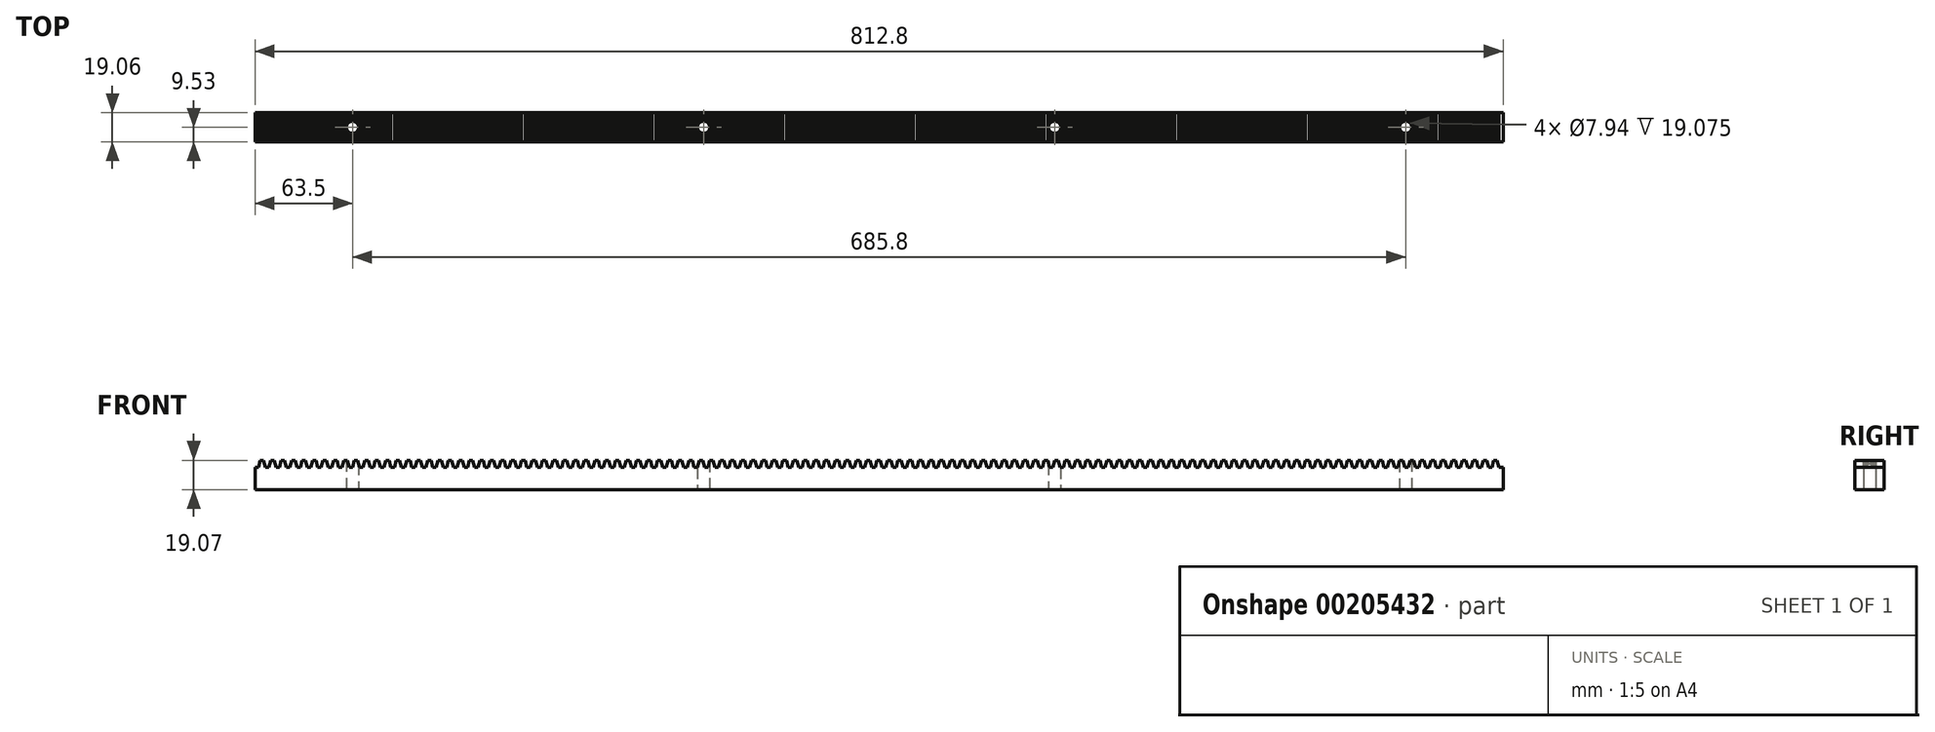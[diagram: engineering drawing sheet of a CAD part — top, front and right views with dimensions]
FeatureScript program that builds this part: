
annotation { "Feature Type Name" : "Feature", "Feature Type Description" : "" }
export const myFeature = defineFeature(function(context is Context, id is Id, definition is map)
    precondition{}
    {
        {
            var Q0;
            Q0=qCreatedBy(makeId("Right.planeOp"),FACE);
            var sketch = newSketch(context, id + "F0", { "sketchPlane" : qUnion([Q0])});
            skLineSegment(sketch, "E0.bottom", {"start": v(-9.52, 7.25) * mm, "end": v(9.53, 7.25) * mm});
            skLineSegment(sketch, "E0.top", {"start": v(-9.53, -7.25) * mm, "end": v(9.52, -7.25) * mm});
            skLineSegment(sketch, "E0.left", {"start": v(-9.52, 7.25) * mm, "end": v(-9.53, -7.25) * mm});
            skLineSegment(sketch, "E0.right", {"start": v(9.53, 7.25) * mm, "end": v(9.52, -7.25) * mm});
            skPoint(sketch, "E0.middle", {"position": v(0, 0) * mm});
            skSolve(sketch);
        }
        {
            var Q0;
            Q0 = qSketchRegion(id + "F0", true);
            extrude(context, id + "F1", {"entities" : qUnion([Q0]), "endBound" : BoundingType.SYMMETRIC, "depth" : 812.8 * mm});
        }
        {
            var Q0;
            Q0=makeQuery(id+"F1.opExtrude","SWEPT_FACE",FACE,{"disambiguationData":[OSD([sQuery(id+"F0.wireOp",EDGE,"E0.left")])]});
            var sketch = newSketch(context, id + "F2", { "sketchPlane" : qUnion([Q0])});
            skLineSegment(sketch, "E1.0", {"start": v(406.4, 7.25) * mm, "end": v(-406.4, 7.25) * mm});
            skLineSegment(sketch, "E2.0", {"start": v(406.4, 11.82) * mm, "end": v(-406.4, 11.82) * mm, "construction": true});
            skLineSegment(sketch, "E3", {"start": v(-406.4, 7.25) * mm, "end": v(-406.4, 19.13) * mm, "construction": true});
            skLineSegment(sketch, "E4.0", {"start": v(-404.16, 7.25) * mm, "end": v(-404.16, 19.13) * mm, "construction": true});
            skLineSegment(sketch, "E5.0", {"start": v(-403, 7.25) * mm, "end": v(-403, 19.13) * mm, "construction": true});
            skLineSegment(sketch, "E6.0", {"start": v(-400.76, 7.25) * mm, "end": v(-400.76, 19.13) * mm, "construction": true});
            skLineSegment(sketch, "E7.0", {"start": v(-399.6, 7.25) * mm, "end": v(-399.6, 19.13) * mm, "construction": true});
            skLineSegment(sketch, "E8", {"start": v(-406.4, 7.25) * mm, "end": v(-404.16, 7.25) * mm});
            skLineSegment(sketch, "E9", {"start": v(-403, 11.82) * mm, "end": v(-404.16, 7.25) * mm});
            skLineSegment(sketch, "E10", {"start": v(-403, 11.82) * mm, "end": v(-400.76, 11.82) * mm});
            skLineSegment(sketch, "E11", {"start": v(-400.76, 11.82) * mm, "end": v(-399.6, 7.25) * mm});
            skLineSegment(sketch, "E12.1.0.0", {"start": v(-399.6, 7.25) * mm, "end": v(-397.36, 7.25) * mm});
            skLineSegment(sketch, "E12.1.0.1", {"start": v(-393.95, 11.82) * mm, "end": v(-392.79, 7.25) * mm});
            skLineSegment(sketch, "E12.1.0.2", {"start": v(-396.19, 11.82) * mm, "end": v(-393.95, 11.82) * mm});
            skLineSegment(sketch, "E12.1.0.3", {"start": v(-396.19, 11.82) * mm, "end": v(-397.36, 7.25) * mm});
            skLineSegment(sketch, "E12.2.0.0", {"start": v(-392.79, 7.25) * mm, "end": v(-390.55, 7.25) * mm});
            skLineSegment(sketch, "E12.2.0.1", {"start": v(-387.15, 11.82) * mm, "end": v(-385.98, 7.25) * mm});
            skLineSegment(sketch, "E12.2.0.2", {"start": v(-389.38, 11.82) * mm, "end": v(-387.15, 11.82) * mm});
            skLineSegment(sketch, "E12.2.0.3", {"start": v(-389.38, 11.82) * mm, "end": v(-390.55, 7.25) * mm});
            skLineSegment(sketch, "E12.3.0.0", {"start": v(-385.98, 7.25) * mm, "end": v(-383.74, 7.25) * mm});
            skLineSegment(sketch, "E12.3.0.1", {"start": v(-380.34, 11.82) * mm, "end": v(-379.17, 7.25) * mm});
            skLineSegment(sketch, "E12.3.0.2", {"start": v(-382.57, 11.82) * mm, "end": v(-380.34, 11.82) * mm});
            skLineSegment(sketch, "E12.3.0.3", {"start": v(-382.57, 11.82) * mm, "end": v(-383.74, 7.25) * mm});
            skLineSegment(sketch, "E12.4.0.0", {"start": v(-379.17, 7.25) * mm, "end": v(-376.94, 7.25) * mm});
            skLineSegment(sketch, "E12.4.0.1", {"start": v(-373.53, 11.82) * mm, "end": v(-372.36, 7.25) * mm});
            skLineSegment(sketch, "E12.4.0.2", {"start": v(-375.77, 11.82) * mm, "end": v(-373.53, 11.82) * mm});
            skLineSegment(sketch, "E12.4.0.3", {"start": v(-375.77, 11.82) * mm, "end": v(-376.94, 7.25) * mm});
            skLineSegment(sketch, "E12.5.0.0", {"start": v(-372.36, 7.25) * mm, "end": v(-370.13, 7.25) * mm});
            skLineSegment(sketch, "E12.5.0.1", {"start": v(-366.73, 11.82) * mm, "end": v(-365.56, 7.25) * mm});
            skLineSegment(sketch, "E12.5.0.2", {"start": v(-368.96, 11.82) * mm, "end": v(-366.73, 11.82) * mm});
            skLineSegment(sketch, "E12.5.0.3", {"start": v(-368.96, 11.82) * mm, "end": v(-370.13, 7.25) * mm});
            skLineSegment(sketch, "E12.6.0.0", {"start": v(-365.56, 7.25) * mm, "end": v(-363.32, 7.25) * mm});
            skLineSegment(sketch, "E12.6.0.1", {"start": v(-359.92, 11.82) * mm, "end": v(-358.75, 7.25) * mm});
            skLineSegment(sketch, "E12.6.0.2", {"start": v(-362.15, 11.82) * mm, "end": v(-359.92, 11.82) * mm});
            skLineSegment(sketch, "E12.6.0.3", {"start": v(-362.15, 11.82) * mm, "end": v(-363.32, 7.25) * mm});
            skLineSegment(sketch, "E12.7.0.0", {"start": v(-358.75, 7.25) * mm, "end": v(-356.51, 7.25) * mm});
            skLineSegment(sketch, "E12.7.0.1", {"start": v(-353.11, 11.82) * mm, "end": v(-351.94, 7.25) * mm});
            skLineSegment(sketch, "E12.7.0.2", {"start": v(-355.35, 11.82) * mm, "end": v(-353.11, 11.82) * mm});
            skLineSegment(sketch, "E12.7.0.3", {"start": v(-355.35, 11.82) * mm, "end": v(-356.51, 7.25) * mm});
            skLineSegment(sketch, "E12.8.0.0", {"start": v(-351.94, 7.25) * mm, "end": v(-349.7, 7.25) * mm});
            skLineSegment(sketch, "E12.8.0.1", {"start": v(-346.3, 11.82) * mm, "end": v(-345.14, 7.25) * mm});
            skLineSegment(sketch, "E12.8.0.2", {"start": v(-348.54, 11.82) * mm, "end": v(-346.3, 11.82) * mm});
            skLineSegment(sketch, "E12.8.0.3", {"start": v(-348.54, 11.82) * mm, "end": v(-349.7, 7.25) * mm});
            skLineSegment(sketch, "E12.9.0.0", {"start": v(-345.14, 7.25) * mm, "end": v(-342.9, 7.25) * mm});
            skLineSegment(sketch, "E12.9.0.1", {"start": v(-339.5, 11.82) * mm, "end": v(-338.33, 7.25) * mm});
            skLineSegment(sketch, "E12.9.0.2", {"start": v(-341.73, 11.82) * mm, "end": v(-339.5, 11.82) * mm});
            skLineSegment(sketch, "E12.9.0.3", {"start": v(-341.73, 11.82) * mm, "end": v(-342.9, 7.25) * mm});
            skLineSegment(sketch, "E12.10.0.0", {"start": v(-338.33, 7.25) * mm, "end": v(-336.1, 7.25) * mm});
            skLineSegment(sketch, "E12.10.0.1", {"start": v(-332.69, 11.82) * mm, "end": v(-331.52, 7.25) * mm});
            skLineSegment(sketch, "E12.10.0.2", {"start": v(-334.92, 11.82) * mm, "end": v(-332.69, 11.82) * mm});
            skLineSegment(sketch, "E12.10.0.3", {"start": v(-334.92, 11.82) * mm, "end": v(-336.1, 7.25) * mm});
            skLineSegment(sketch, "E12.11.0.0", {"start": v(-331.52, 7.25) * mm, "end": v(-329.29, 7.25) * mm});
            skLineSegment(sketch, "E12.11.0.1", {"start": v(-325.88, 11.82) * mm, "end": v(-324.71, 7.25) * mm});
            skLineSegment(sketch, "E12.11.0.2", {"start": v(-328.12, 11.82) * mm, "end": v(-325.88, 11.82) * mm});
            skLineSegment(sketch, "E12.11.0.3", {"start": v(-328.12, 11.82) * mm, "end": v(-329.29, 7.25) * mm});
            skLineSegment(sketch, "E12.12.0.0", {"start": v(-324.71, 7.25) * mm, "end": v(-322.48, 7.25) * mm});
            skLineSegment(sketch, "E12.12.0.1", {"start": v(-319.07, 11.82) * mm, "end": v(-317.9, 7.25) * mm});
            skLineSegment(sketch, "E12.12.0.2", {"start": v(-321.3, 11.82) * mm, "end": v(-319.07, 11.82) * mm});
            skLineSegment(sketch, "E12.12.0.3", {"start": v(-321.3, 11.82) * mm, "end": v(-322.48, 7.25) * mm});
            skLineSegment(sketch, "E12.13.0.0", {"start": v(-317.9, 7.25) * mm, "end": v(-315.67, 7.25) * mm});
            skLineSegment(sketch, "E12.13.0.1", {"start": v(-312.27, 11.82) * mm, "end": v(-311.1, 7.25) * mm});
            skLineSegment(sketch, "E12.13.0.2", {"start": v(-314.5, 11.82) * mm, "end": v(-312.27, 11.82) * mm});
            skLineSegment(sketch, "E12.13.0.3", {"start": v(-314.5, 11.82) * mm, "end": v(-315.67, 7.25) * mm});
            skLineSegment(sketch, "E12.14.0.0", {"start": v(-311.1, 7.25) * mm, "end": v(-308.86, 7.25) * mm});
            skLineSegment(sketch, "E12.14.0.1", {"start": v(-305.46, 11.82) * mm, "end": v(-304.3, 7.25) * mm});
            skLineSegment(sketch, "E12.14.0.2", {"start": v(-307.7, 11.82) * mm, "end": v(-305.46, 11.82) * mm});
            skLineSegment(sketch, "E12.14.0.3", {"start": v(-307.7, 11.82) * mm, "end": v(-308.86, 7.25) * mm});
            skLineSegment(sketch, "E12.15.0.0", {"start": v(-304.3, 7.25) * mm, "end": v(-302.06, 7.25) * mm});
            skLineSegment(sketch, "E12.15.0.1", {"start": v(-298.65, 11.82) * mm, "end": v(-297.48, 7.25) * mm});
            skLineSegment(sketch, "E12.15.0.2", {"start": v(-300.89, 11.82) * mm, "end": v(-298.65, 11.82) * mm});
            skLineSegment(sketch, "E12.15.0.3", {"start": v(-300.89, 11.82) * mm, "end": v(-302.06, 7.25) * mm});
            skLineSegment(sketch, "E12.16.0.0", {"start": v(-297.48, 7.25) * mm, "end": v(-295.25, 7.25) * mm});
            skLineSegment(sketch, "E12.16.0.1", {"start": v(-291.85, 11.82) * mm, "end": v(-290.68, 7.25) * mm});
            skLineSegment(sketch, "E12.16.0.2", {"start": v(-294.08, 11.82) * mm, "end": v(-291.85, 11.82) * mm});
            skLineSegment(sketch, "E12.16.0.3", {"start": v(-294.08, 11.82) * mm, "end": v(-295.25, 7.25) * mm});
            skLineSegment(sketch, "E12.17.0.0", {"start": v(-290.68, 7.25) * mm, "end": v(-288.44, 7.25) * mm});
            skLineSegment(sketch, "E12.17.0.1", {"start": v(-285.04, 11.82) * mm, "end": v(-283.87, 7.25) * mm});
            skLineSegment(sketch, "E12.17.0.2", {"start": v(-287.27, 11.82) * mm, "end": v(-285.04, 11.82) * mm});
            skLineSegment(sketch, "E12.17.0.3", {"start": v(-287.27, 11.82) * mm, "end": v(-288.44, 7.25) * mm});
            skLineSegment(sketch, "E12.18.0.0", {"start": v(-283.87, 7.25) * mm, "end": v(-281.64, 7.25) * mm});
            skLineSegment(sketch, "E12.18.0.1", {"start": v(-278.23, 11.82) * mm, "end": v(-277.06, 7.25) * mm});
            skLineSegment(sketch, "E12.18.0.2", {"start": v(-280.47, 11.82) * mm, "end": v(-278.23, 11.82) * mm});
            skLineSegment(sketch, "E12.18.0.3", {"start": v(-280.47, 11.82) * mm, "end": v(-281.64, 7.25) * mm});
            skLineSegment(sketch, "E12.19.0.0", {"start": v(-277.06, 7.25) * mm, "end": v(-274.83, 7.25) * mm});
            skLineSegment(sketch, "E12.19.0.1", {"start": v(-271.42, 11.82) * mm, "end": v(-270.26, 7.25) * mm});
            skLineSegment(sketch, "E12.19.0.2", {"start": v(-273.66, 11.82) * mm, "end": v(-271.42, 11.82) * mm});
            skLineSegment(sketch, "E12.19.0.3", {"start": v(-273.66, 11.82) * mm, "end": v(-274.83, 7.25) * mm});
            skLineSegment(sketch, "E12.direction1", {"start": v(-406.4, 7.25) * mm, "end": v(-399.6, 7.25) * mm, "construction": true});
            skLineSegment(sketch, "E13.1.0.0", {"start": v(-264.62, 11.82) * mm, "end": v(-263.45, 7.25) * mm});
            skLineSegment(sketch, "E13.1.0.1", {"start": v(-266.85, 11.82) * mm, "end": v(-264.62, 11.82) * mm});
            skLineSegment(sketch, "E13.1.0.2", {"start": v(-266.85, 11.82) * mm, "end": v(-268.02, 7.25) * mm});
            skLineSegment(sketch, "E13.1.0.3", {"start": v(-270.26, 7.25) * mm, "end": v(-268.02, 7.25) * mm});
            skLineSegment(sketch, "E13.2.0.0", {"start": v(-257.8, 11.82) * mm, "end": v(-256.64, 7.25) * mm});
            skLineSegment(sketch, "E13.2.0.1", {"start": v(-260.05, 11.82) * mm, "end": v(-257.8, 11.82) * mm});
            skLineSegment(sketch, "E13.2.0.2", {"start": v(-260.05, 11.82) * mm, "end": v(-261.21, 7.25) * mm});
            skLineSegment(sketch, "E13.2.0.3", {"start": v(-263.45, 7.25) * mm, "end": v(-261.21, 7.25) * mm});
            skLineSegment(sketch, "E13.3.0.0", {"start": v(-251, 11.82) * mm, "end": v(-249.83, 7.25) * mm});
            skLineSegment(sketch, "E13.3.0.1", {"start": v(-253.24, 11.82) * mm, "end": v(-251, 11.82) * mm});
            skLineSegment(sketch, "E13.3.0.2", {"start": v(-253.24, 11.82) * mm, "end": v(-254.4, 7.25) * mm});
            skLineSegment(sketch, "E13.3.0.3", {"start": v(-256.64, 7.25) * mm, "end": v(-254.4, 7.25) * mm});
            skLineSegment(sketch, "E13.4.0.0", {"start": v(-244.2, 11.82) * mm, "end": v(-243.03, 7.25) * mm});
            skLineSegment(sketch, "E13.4.0.1", {"start": v(-246.43, 11.82) * mm, "end": v(-244.2, 11.82) * mm});
            skLineSegment(sketch, "E13.4.0.2", {"start": v(-246.43, 11.82) * mm, "end": v(-247.6, 7.25) * mm});
            skLineSegment(sketch, "E13.4.0.3", {"start": v(-249.83, 7.25) * mm, "end": v(-247.6, 7.25) * mm});
            skLineSegment(sketch, "E13.5.0.0", {"start": v(-237.39, 11.82) * mm, "end": v(-236.22, 7.25) * mm});
            skLineSegment(sketch, "E13.5.0.1", {"start": v(-239.62, 11.82) * mm, "end": v(-237.39, 11.82) * mm});
            skLineSegment(sketch, "E13.5.0.2", {"start": v(-239.62, 11.82) * mm, "end": v(-240.8, 7.25) * mm});
            skLineSegment(sketch, "E13.5.0.3", {"start": v(-243.03, 7.25) * mm, "end": v(-240.8, 7.25) * mm});
            skLineSegment(sketch, "E13.6.0.0", {"start": v(-230.58, 11.82) * mm, "end": v(-229.41, 7.25) * mm});
            skLineSegment(sketch, "E13.6.0.1", {"start": v(-232.82, 11.82) * mm, "end": v(-230.58, 11.82) * mm});
            skLineSegment(sketch, "E13.6.0.2", {"start": v(-232.82, 11.82) * mm, "end": v(-233.98, 7.25) * mm});
            skLineSegment(sketch, "E13.6.0.3", {"start": v(-236.22, 7.25) * mm, "end": v(-233.98, 7.25) * mm});
            skLineSegment(sketch, "E13.7.0.0", {"start": v(-223.77, 11.82) * mm, "end": v(-222.6, 7.25) * mm});
            skLineSegment(sketch, "E13.7.0.1", {"start": v(-226, 11.82) * mm, "end": v(-223.77, 11.82) * mm});
            skLineSegment(sketch, "E13.7.0.2", {"start": v(-226, 11.82) * mm, "end": v(-227.18, 7.25) * mm});
            skLineSegment(sketch, "E13.7.0.3", {"start": v(-229.41, 7.25) * mm, "end": v(-227.18, 7.25) * mm});
            skLineSegment(sketch, "E13.8.0.0", {"start": v(-216.97, 11.82) * mm, "end": v(-215.8, 7.25) * mm});
            skLineSegment(sketch, "E13.8.0.1", {"start": v(-219.2, 11.82) * mm, "end": v(-216.97, 11.82) * mm});
            skLineSegment(sketch, "E13.8.0.2", {"start": v(-219.2, 11.82) * mm, "end": v(-220.37, 7.25) * mm});
            skLineSegment(sketch, "E13.8.0.3", {"start": v(-222.6, 7.25) * mm, "end": v(-220.37, 7.25) * mm});
            skLineSegment(sketch, "E13.9.0.0", {"start": v(-210.16, 11.82) * mm, "end": v(-209, 7.25) * mm});
            skLineSegment(sketch, "E13.9.0.1", {"start": v(-212.4, 11.82) * mm, "end": v(-210.16, 11.82) * mm});
            skLineSegment(sketch, "E13.9.0.2", {"start": v(-212.4, 11.82) * mm, "end": v(-213.56, 7.25) * mm});
            skLineSegment(sketch, "E13.9.0.3", {"start": v(-215.8, 7.25) * mm, "end": v(-213.56, 7.25) * mm});
            skLineSegment(sketch, "E13.10.0.0", {"start": v(-203.35, 11.82) * mm, "end": v(-202.18, 7.25) * mm});
            skLineSegment(sketch, "E13.10.0.1", {"start": v(-205.59, 11.82) * mm, "end": v(-203.35, 11.82) * mm});
            skLineSegment(sketch, "E13.10.0.2", {"start": v(-205.59, 11.82) * mm, "end": v(-206.76, 7.25) * mm});
            skLineSegment(sketch, "E13.10.0.3", {"start": v(-209, 7.25) * mm, "end": v(-206.76, 7.25) * mm});
            skLineSegment(sketch, "E13.11.0.0", {"start": v(-196.55, 11.82) * mm, "end": v(-195.38, 7.25) * mm});
            skLineSegment(sketch, "E13.11.0.1", {"start": v(-198.78, 11.82) * mm, "end": v(-196.55, 11.82) * mm});
            skLineSegment(sketch, "E13.11.0.2", {"start": v(-198.78, 11.82) * mm, "end": v(-199.95, 7.25) * mm});
            skLineSegment(sketch, "E13.11.0.3", {"start": v(-202.18, 7.25) * mm, "end": v(-199.95, 7.25) * mm});
            skLineSegment(sketch, "E13.12.0.0", {"start": v(-189.74, 11.82) * mm, "end": v(-188.57, 7.25) * mm});
            skLineSegment(sketch, "E13.12.0.1", {"start": v(-191.97, 11.82) * mm, "end": v(-189.74, 11.82) * mm});
            skLineSegment(sketch, "E13.12.0.2", {"start": v(-191.97, 11.82) * mm, "end": v(-193.14, 7.25) * mm});
            skLineSegment(sketch, "E13.12.0.3", {"start": v(-195.38, 7.25) * mm, "end": v(-193.14, 7.25) * mm});
            skLineSegment(sketch, "E13.13.0.0", {"start": v(-182.93, 11.82) * mm, "end": v(-181.76, 7.25) * mm});
            skLineSegment(sketch, "E13.13.0.1", {"start": v(-185.17, 11.82) * mm, "end": v(-182.93, 11.82) * mm});
            skLineSegment(sketch, "E13.13.0.2", {"start": v(-185.17, 11.82) * mm, "end": v(-186.33, 7.25) * mm});
            skLineSegment(sketch, "E13.13.0.3", {"start": v(-188.57, 7.25) * mm, "end": v(-186.33, 7.25) * mm});
            skLineSegment(sketch, "E13.14.0.0", {"start": v(-176.12, 11.82) * mm, "end": v(-174.96, 7.25) * mm});
            skLineSegment(sketch, "E13.14.0.1", {"start": v(-178.36, 11.82) * mm, "end": v(-176.12, 11.82) * mm});
            skLineSegment(sketch, "E13.14.0.2", {"start": v(-178.36, 11.82) * mm, "end": v(-179.53, 7.25) * mm});
            skLineSegment(sketch, "E13.14.0.3", {"start": v(-181.76, 7.25) * mm, "end": v(-179.53, 7.25) * mm});
            skLineSegment(sketch, "E13.15.0.0", {"start": v(-169.32, 11.82) * mm, "end": v(-168.15, 7.25) * mm});
            skLineSegment(sketch, "E13.15.0.1", {"start": v(-171.55, 11.82) * mm, "end": v(-169.32, 11.82) * mm});
            skLineSegment(sketch, "E13.15.0.2", {"start": v(-171.55, 11.82) * mm, "end": v(-172.72, 7.25) * mm});
            skLineSegment(sketch, "E13.15.0.3", {"start": v(-174.96, 7.25) * mm, "end": v(-172.72, 7.25) * mm});
            skLineSegment(sketch, "E13.16.0.0", {"start": v(-162.5, 11.82) * mm, "end": v(-161.34, 7.25) * mm});
            skLineSegment(sketch, "E13.16.0.1", {"start": v(-164.74, 11.82) * mm, "end": v(-162.5, 11.82) * mm});
            skLineSegment(sketch, "E13.16.0.2", {"start": v(-164.74, 11.82) * mm, "end": v(-165.91, 7.25) * mm});
            skLineSegment(sketch, "E13.16.0.3", {"start": v(-168.15, 7.25) * mm, "end": v(-165.91, 7.25) * mm});
            skLineSegment(sketch, "E13.17.0.0", {"start": v(-155.7, 11.82) * mm, "end": v(-154.53, 7.25) * mm});
            skLineSegment(sketch, "E13.17.0.1", {"start": v(-157.94, 11.82) * mm, "end": v(-155.7, 11.82) * mm});
            skLineSegment(sketch, "E13.17.0.2", {"start": v(-157.94, 11.82) * mm, "end": v(-159.1, 7.25) * mm});
            skLineSegment(sketch, "E13.17.0.3", {"start": v(-161.34, 7.25) * mm, "end": v(-159.1, 7.25) * mm});
            skLineSegment(sketch, "E13.18.0.0", {"start": v(-148.9, 11.82) * mm, "end": v(-147.73, 7.25) * mm});
            skLineSegment(sketch, "E13.18.0.1", {"start": v(-151.13, 11.82) * mm, "end": v(-148.9, 11.82) * mm});
            skLineSegment(sketch, "E13.18.0.2", {"start": v(-151.13, 11.82) * mm, "end": v(-152.3, 7.25) * mm});
            skLineSegment(sketch, "E13.18.0.3", {"start": v(-154.53, 7.25) * mm, "end": v(-152.3, 7.25) * mm});
            skLineSegment(sketch, "E13.19.0.0", {"start": v(-142.09, 11.82) * mm, "end": v(-140.92, 7.25) * mm});
            skLineSegment(sketch, "E13.19.0.1", {"start": v(-144.32, 11.82) * mm, "end": v(-142.09, 11.82) * mm});
            skLineSegment(sketch, "E13.19.0.2", {"start": v(-144.32, 11.82) * mm, "end": v(-145.5, 7.25) * mm});
            skLineSegment(sketch, "E13.19.0.3", {"start": v(-147.73, 7.25) * mm, "end": v(-145.5, 7.25) * mm});
            skLineSegment(sketch, "E13.direction1", {"start": v(-277.06, 7.25) * mm, "end": v(-270.26, 7.25) * mm, "construction": true});
            skLineSegment(sketch, "E14.1.0.0", {"start": v(-140.92, 7.25) * mm, "end": v(-138.68, 7.25) * mm});
            skLineSegment(sketch, "E14.1.0.1", {"start": v(-135.28, 11.82) * mm, "end": v(-134.11, 7.25) * mm});
            skLineSegment(sketch, "E14.1.0.2", {"start": v(-137.52, 11.82) * mm, "end": v(-138.68, 7.25) * mm});
            skLineSegment(sketch, "E14.1.0.3", {"start": v(-137.52, 11.82) * mm, "end": v(-135.28, 11.82) * mm});
            skLineSegment(sketch, "E14.2.0.0", {"start": v(-134.11, 7.25) * mm, "end": v(-131.88, 7.25) * mm});
            skLineSegment(sketch, "E14.2.0.1", {"start": v(-128.47, 11.82) * mm, "end": v(-127.3, 7.25) * mm});
            skLineSegment(sketch, "E14.2.0.2", {"start": v(-130.7, 11.82) * mm, "end": v(-131.88, 7.25) * mm});
            skLineSegment(sketch, "E14.2.0.3", {"start": v(-130.7, 11.82) * mm, "end": v(-128.47, 11.82) * mm});
            skLineSegment(sketch, "E14.3.0.0", {"start": v(-127.3, 7.25) * mm, "end": v(-125.07, 7.25) * mm});
            skLineSegment(sketch, "E14.3.0.1", {"start": v(-121.67, 11.82) * mm, "end": v(-120.5, 7.25) * mm});
            skLineSegment(sketch, "E14.3.0.2", {"start": v(-123.9, 11.82) * mm, "end": v(-125.07, 7.25) * mm});
            skLineSegment(sketch, "E14.3.0.3", {"start": v(-123.9, 11.82) * mm, "end": v(-121.67, 11.82) * mm});
            skLineSegment(sketch, "E14.4.0.0", {"start": v(-120.5, 7.25) * mm, "end": v(-118.26, 7.25) * mm});
            skLineSegment(sketch, "E14.4.0.1", {"start": v(-114.86, 11.82) * mm, "end": v(-113.7, 7.25) * mm});
            skLineSegment(sketch, "E14.4.0.2", {"start": v(-117.1, 11.82) * mm, "end": v(-118.26, 7.25) * mm});
            skLineSegment(sketch, "E14.4.0.3", {"start": v(-117.1, 11.82) * mm, "end": v(-114.86, 11.82) * mm});
            skLineSegment(sketch, "E14.5.0.0", {"start": v(-113.7, 7.25) * mm, "end": v(-111.46, 7.25) * mm});
            skLineSegment(sketch, "E14.5.0.1", {"start": v(-108.05, 11.82) * mm, "end": v(-106.88, 7.25) * mm});
            skLineSegment(sketch, "E14.5.0.2", {"start": v(-110.29, 11.82) * mm, "end": v(-111.46, 7.25) * mm});
            skLineSegment(sketch, "E14.5.0.3", {"start": v(-110.29, 11.82) * mm, "end": v(-108.05, 11.82) * mm});
            skLineSegment(sketch, "E14.6.0.0", {"start": v(-106.88, 7.25) * mm, "end": v(-104.65, 7.25) * mm});
            skLineSegment(sketch, "E14.6.0.1", {"start": v(-101.24, 11.82) * mm, "end": v(-100.08, 7.25) * mm});
            skLineSegment(sketch, "E14.6.0.2", {"start": v(-103.48, 11.82) * mm, "end": v(-104.65, 7.25) * mm});
            skLineSegment(sketch, "E14.6.0.3", {"start": v(-103.48, 11.82) * mm, "end": v(-101.24, 11.82) * mm});
            skLineSegment(sketch, "E14.7.0.0", {"start": v(-100.08, 7.25) * mm, "end": v(-97.84, 7.25) * mm});
            skLineSegment(sketch, "E14.7.0.1", {"start": v(-94.44, 11.82) * mm, "end": v(-93.27, 7.25) * mm});
            skLineSegment(sketch, "E14.7.0.2", {"start": v(-96.67, 11.82) * mm, "end": v(-97.84, 7.25) * mm});
            skLineSegment(sketch, "E14.7.0.3", {"start": v(-96.67, 11.82) * mm, "end": v(-94.44, 11.82) * mm});
            skLineSegment(sketch, "E14.8.0.0", {"start": v(-93.27, 7.25) * mm, "end": v(-91.03, 7.25) * mm});
            skLineSegment(sketch, "E14.8.0.1", {"start": v(-87.63, 11.82) * mm, "end": v(-86.46, 7.25) * mm});
            skLineSegment(sketch, "E14.8.0.2", {"start": v(-89.87, 11.82) * mm, "end": v(-91.03, 7.25) * mm});
            skLineSegment(sketch, "E14.8.0.3", {"start": v(-89.87, 11.82) * mm, "end": v(-87.63, 11.82) * mm});
            skLineSegment(sketch, "E14.9.0.0", {"start": v(-86.46, 7.25) * mm, "end": v(-84.23, 7.25) * mm});
            skLineSegment(sketch, "E14.9.0.1", {"start": v(-80.82, 11.82) * mm, "end": v(-79.65, 7.25) * mm});
            skLineSegment(sketch, "E14.9.0.2", {"start": v(-83.06, 11.82) * mm, "end": v(-84.23, 7.25) * mm});
            skLineSegment(sketch, "E14.9.0.3", {"start": v(-83.06, 11.82) * mm, "end": v(-80.82, 11.82) * mm});
            skLineSegment(sketch, "E14.10.0.0", {"start": v(-79.65, 7.25) * mm, "end": v(-77.42, 7.25) * mm});
            skLineSegment(sketch, "E14.10.0.1", {"start": v(-74.02, 11.82) * mm, "end": v(-72.85, 7.25) * mm});
            skLineSegment(sketch, "E14.10.0.2", {"start": v(-76.25, 11.82) * mm, "end": v(-77.42, 7.25) * mm});
            skLineSegment(sketch, "E14.10.0.3", {"start": v(-76.25, 11.82) * mm, "end": v(-74.02, 11.82) * mm});
            skLineSegment(sketch, "E14.11.0.0", {"start": v(-72.85, 7.25) * mm, "end": v(-70.61, 7.25) * mm});
            skLineSegment(sketch, "E14.11.0.1", {"start": v(-67.2, 11.82) * mm, "end": v(-66.04, 7.25) * mm});
            skLineSegment(sketch, "E14.11.0.2", {"start": v(-69.44, 11.82) * mm, "end": v(-70.61, 7.25) * mm});
            skLineSegment(sketch, "E14.11.0.3", {"start": v(-69.44, 11.82) * mm, "end": v(-67.2, 11.82) * mm});
            skLineSegment(sketch, "E14.12.0.0", {"start": v(-66.04, 7.25) * mm, "end": v(-63.8, 7.25) * mm});
            skLineSegment(sketch, "E14.12.0.1", {"start": v(-60.4, 11.82) * mm, "end": v(-59.23, 7.25) * mm});
            skLineSegment(sketch, "E14.12.0.2", {"start": v(-62.64, 11.82) * mm, "end": v(-63.8, 7.25) * mm});
            skLineSegment(sketch, "E14.12.0.3", {"start": v(-62.64, 11.82) * mm, "end": v(-60.4, 11.82) * mm});
            skLineSegment(sketch, "E14.13.0.0", {"start": v(-59.23, 7.25) * mm, "end": v(-57, 7.25) * mm});
            skLineSegment(sketch, "E14.13.0.1", {"start": v(-53.6, 11.82) * mm, "end": v(-52.43, 7.25) * mm});
            skLineSegment(sketch, "E14.13.0.2", {"start": v(-55.83, 11.82) * mm, "end": v(-57, 7.25) * mm});
            skLineSegment(sketch, "E14.13.0.3", {"start": v(-55.83, 11.82) * mm, "end": v(-53.6, 11.82) * mm});
            skLineSegment(sketch, "E14.14.0.0", {"start": v(-52.43, 7.25) * mm, "end": v(-50.2, 7.25) * mm});
            skLineSegment(sketch, "E14.14.0.1", {"start": v(-46.79, 11.82) * mm, "end": v(-45.62, 7.25) * mm});
            skLineSegment(sketch, "E14.14.0.2", {"start": v(-49.02, 11.82) * mm, "end": v(-50.2, 7.25) * mm});
            skLineSegment(sketch, "E14.14.0.3", {"start": v(-49.02, 11.82) * mm, "end": v(-46.79, 11.82) * mm});
            skLineSegment(sketch, "E14.15.0.0", {"start": v(-45.62, 7.25) * mm, "end": v(-43.38, 7.25) * mm});
            skLineSegment(sketch, "E14.15.0.1", {"start": v(-39.98, 11.82) * mm, "end": v(-38.81, 7.25) * mm});
            skLineSegment(sketch, "E14.15.0.2", {"start": v(-42.21, 11.82) * mm, "end": v(-43.38, 7.25) * mm});
            skLineSegment(sketch, "E14.15.0.3", {"start": v(-42.21, 11.82) * mm, "end": v(-39.98, 11.82) * mm});
            skLineSegment(sketch, "E14.16.0.0", {"start": v(-38.81, 7.25) * mm, "end": v(-36.58, 7.25) * mm});
            skLineSegment(sketch, "E14.16.0.1", {"start": v(-33.17, 11.82) * mm, "end": v(-32, 7.25) * mm});
            skLineSegment(sketch, "E14.16.0.2", {"start": v(-35.4, 11.82) * mm, "end": v(-36.58, 7.25) * mm});
            skLineSegment(sketch, "E14.16.0.3", {"start": v(-35.4, 11.82) * mm, "end": v(-33.17, 11.82) * mm});
            skLineSegment(sketch, "E14.17.0.0", {"start": v(-32, 7.25) * mm, "end": v(-29.77, 7.25) * mm});
            skLineSegment(sketch, "E14.17.0.1", {"start": v(-26.37, 11.82) * mm, "end": v(-25.2, 7.25) * mm});
            skLineSegment(sketch, "E14.17.0.2", {"start": v(-28.6, 11.82) * mm, "end": v(-29.77, 7.25) * mm});
            skLineSegment(sketch, "E14.17.0.3", {"start": v(-28.6, 11.82) * mm, "end": v(-26.37, 11.82) * mm});
            skLineSegment(sketch, "E14.18.0.0", {"start": v(-25.2, 7.25) * mm, "end": v(-22.96, 7.25) * mm});
            skLineSegment(sketch, "E14.18.0.1", {"start": v(-19.56, 11.82) * mm, "end": v(-18.39, 7.25) * mm});
            skLineSegment(sketch, "E14.18.0.2", {"start": v(-21.8, 11.82) * mm, "end": v(-22.96, 7.25) * mm});
            skLineSegment(sketch, "E14.18.0.3", {"start": v(-21.8, 11.82) * mm, "end": v(-19.56, 11.82) * mm});
            skLineSegment(sketch, "E14.19.0.0", {"start": v(-18.39, 7.25) * mm, "end": v(-16.15, 7.25) * mm});
            skLineSegment(sketch, "E14.19.0.1", {"start": v(-12.75, 11.82) * mm, "end": v(-11.58, 7.25) * mm});
            skLineSegment(sketch, "E14.19.0.2", {"start": v(-14.99, 11.82) * mm, "end": v(-16.15, 7.25) * mm});
            skLineSegment(sketch, "E14.19.0.3", {"start": v(-14.99, 11.82) * mm, "end": v(-12.75, 11.82) * mm});
            skLineSegment(sketch, "E14.20.0.0", {"start": v(-11.58, 7.25) * mm, "end": v(-9.35, 7.25) * mm});
            skLineSegment(sketch, "E14.20.0.1", {"start": v(-5.94, 11.82) * mm, "end": v(-4.78, 7.25) * mm});
            skLineSegment(sketch, "E14.20.0.2", {"start": v(-8.18, 11.82) * mm, "end": v(-9.35, 7.25) * mm});
            skLineSegment(sketch, "E14.20.0.3", {"start": v(-8.18, 11.82) * mm, "end": v(-5.94, 11.82) * mm});
            skLineSegment(sketch, "E14.21.0.0", {"start": v(-4.78, 7.25) * mm, "end": v(-2.54, 7.25) * mm});
            skLineSegment(sketch, "E14.21.0.1", {"start": v(0.86, 11.82) * mm, "end": v(2.03, 7.25) * mm});
            skLineSegment(sketch, "E14.21.0.2", {"start": v(-1.37, 11.82) * mm, "end": v(-2.54, 7.25) * mm});
            skLineSegment(sketch, "E14.21.0.3", {"start": v(-1.37, 11.82) * mm, "end": v(0.86, 11.82) * mm});
            skLineSegment(sketch, "E14.22.0.0", {"start": v(2.03, 7.25) * mm, "end": v(4.27, 7.25) * mm});
            skLineSegment(sketch, "E14.22.0.1", {"start": v(7.67, 11.82) * mm, "end": v(8.84, 7.25) * mm});
            skLineSegment(sketch, "E14.22.0.2", {"start": v(5.44, 11.82) * mm, "end": v(4.27, 7.25) * mm});
            skLineSegment(sketch, "E14.22.0.3", {"start": v(5.44, 11.82) * mm, "end": v(7.67, 11.82) * mm});
            skLineSegment(sketch, "E14.23.0.0", {"start": v(8.84, 7.25) * mm, "end": v(11.07, 7.25) * mm});
            skLineSegment(sketch, "E14.23.0.1", {"start": v(14.48, 11.82) * mm, "end": v(15.65, 7.25) * mm});
            skLineSegment(sketch, "E14.23.0.2", {"start": v(12.24, 11.82) * mm, "end": v(11.07, 7.25) * mm});
            skLineSegment(sketch, "E14.23.0.3", {"start": v(12.24, 11.82) * mm, "end": v(14.48, 11.82) * mm});
            skLineSegment(sketch, "E14.24.0.0", {"start": v(15.65, 7.25) * mm, "end": v(17.88, 7.25) * mm});
            skLineSegment(sketch, "E14.24.0.1", {"start": v(21.29, 11.82) * mm, "end": v(22.45, 7.25) * mm});
            skLineSegment(sketch, "E14.24.0.2", {"start": v(19.05, 11.82) * mm, "end": v(17.88, 7.25) * mm});
            skLineSegment(sketch, "E14.24.0.3", {"start": v(19.05, 11.82) * mm, "end": v(21.29, 11.82) * mm});
            skLineSegment(sketch, "E14.25.0.0", {"start": v(22.45, 7.25) * mm, "end": v(24.69, 7.25) * mm});
            skLineSegment(sketch, "E14.25.0.1", {"start": v(28.1, 11.82) * mm, "end": v(29.26, 7.25) * mm});
            skLineSegment(sketch, "E14.25.0.2", {"start": v(25.86, 11.82) * mm, "end": v(24.69, 7.25) * mm});
            skLineSegment(sketch, "E14.25.0.3", {"start": v(25.86, 11.82) * mm, "end": v(28.1, 11.82) * mm});
            skLineSegment(sketch, "E14.26.0.0", {"start": v(29.26, 7.25) * mm, "end": v(31.5, 7.25) * mm});
            skLineSegment(sketch, "E14.26.0.1", {"start": v(34.9, 11.82) * mm, "end": v(36.07, 7.25) * mm});
            skLineSegment(sketch, "E14.26.0.2", {"start": v(32.66, 11.82) * mm, "end": v(31.5, 7.25) * mm});
            skLineSegment(sketch, "E14.26.0.3", {"start": v(32.66, 11.82) * mm, "end": v(34.9, 11.82) * mm});
            skLineSegment(sketch, "E14.27.0.0", {"start": v(36.07, 7.25) * mm, "end": v(38.3, 7.25) * mm});
            skLineSegment(sketch, "E14.27.0.1", {"start": v(41.7, 11.82) * mm, "end": v(42.88, 7.25) * mm});
            skLineSegment(sketch, "E14.27.0.2", {"start": v(39.47, 11.82) * mm, "end": v(38.3, 7.25) * mm});
            skLineSegment(sketch, "E14.27.0.3", {"start": v(39.47, 11.82) * mm, "end": v(41.7, 11.82) * mm});
            skLineSegment(sketch, "E14.28.0.0", {"start": v(42.88, 7.25) * mm, "end": v(45.11, 7.25) * mm});
            skLineSegment(sketch, "E14.28.0.1", {"start": v(48.51, 11.82) * mm, "end": v(49.68, 7.25) * mm});
            skLineSegment(sketch, "E14.28.0.2", {"start": v(46.28, 11.82) * mm, "end": v(45.11, 7.25) * mm});
            skLineSegment(sketch, "E14.28.0.3", {"start": v(46.28, 11.82) * mm, "end": v(48.51, 11.82) * mm});
            skLineSegment(sketch, "E14.29.0.0", {"start": v(49.68, 7.25) * mm, "end": v(51.92, 7.25) * mm});
            skLineSegment(sketch, "E14.29.0.1", {"start": v(55.32, 11.82) * mm, "end": v(56.49, 7.25) * mm});
            skLineSegment(sketch, "E14.29.0.2", {"start": v(53.09, 11.82) * mm, "end": v(51.92, 7.25) * mm});
            skLineSegment(sketch, "E14.29.0.3", {"start": v(53.09, 11.82) * mm, "end": v(55.32, 11.82) * mm});
            skLineSegment(sketch, "E14.30.0.0", {"start": v(56.49, 7.25) * mm, "end": v(58.72, 7.25) * mm});
            skLineSegment(sketch, "E14.30.0.1", {"start": v(62.13, 11.82) * mm, "end": v(63.3, 7.25) * mm});
            skLineSegment(sketch, "E14.30.0.2", {"start": v(59.9, 11.82) * mm, "end": v(58.72, 7.25) * mm});
            skLineSegment(sketch, "E14.30.0.3", {"start": v(59.9, 11.82) * mm, "end": v(62.13, 11.82) * mm});
            skLineSegment(sketch, "E14.31.0.0", {"start": v(63.3, 7.25) * mm, "end": v(65.53, 7.25) * mm});
            skLineSegment(sketch, "E14.31.0.1", {"start": v(68.94, 11.82) * mm, "end": v(70.1, 7.25) * mm});
            skLineSegment(sketch, "E14.31.0.2", {"start": v(66.7, 11.82) * mm, "end": v(65.53, 7.25) * mm});
            skLineSegment(sketch, "E14.31.0.3", {"start": v(66.7, 11.82) * mm, "end": v(68.94, 11.82) * mm});
            skLineSegment(sketch, "E14.32.0.0", {"start": v(70.1, 7.25) * mm, "end": v(72.34, 7.25) * mm});
            skLineSegment(sketch, "E14.32.0.1", {"start": v(75.74, 11.82) * mm, "end": v(76.91, 7.25) * mm});
            skLineSegment(sketch, "E14.32.0.2", {"start": v(73.5, 11.82) * mm, "end": v(72.34, 7.25) * mm});
            skLineSegment(sketch, "E14.32.0.3", {"start": v(73.5, 11.82) * mm, "end": v(75.74, 11.82) * mm});
            skLineSegment(sketch, "E14.33.0.0", {"start": v(76.91, 7.25) * mm, "end": v(79.15, 7.25) * mm});
            skLineSegment(sketch, "E14.33.0.1", {"start": v(82.55, 11.82) * mm, "end": v(83.72, 7.25) * mm});
            skLineSegment(sketch, "E14.33.0.2", {"start": v(80.31, 11.82) * mm, "end": v(79.15, 7.25) * mm});
            skLineSegment(sketch, "E14.33.0.3", {"start": v(80.31, 11.82) * mm, "end": v(82.55, 11.82) * mm});
            skLineSegment(sketch, "E14.34.0.0", {"start": v(83.72, 7.25) * mm, "end": v(85.95, 7.25) * mm});
            skLineSegment(sketch, "E14.34.0.1", {"start": v(89.36, 11.82) * mm, "end": v(90.53, 7.25) * mm});
            skLineSegment(sketch, "E14.34.0.2", {"start": v(87.12, 11.82) * mm, "end": v(85.95, 7.25) * mm});
            skLineSegment(sketch, "E14.34.0.3", {"start": v(87.12, 11.82) * mm, "end": v(89.36, 11.82) * mm});
            skLineSegment(sketch, "E14.35.0.0", {"start": v(90.53, 7.25) * mm, "end": v(92.76, 7.25) * mm});
            skLineSegment(sketch, "E14.35.0.1", {"start": v(96.16, 11.82) * mm, "end": v(97.33, 7.25) * mm});
            skLineSegment(sketch, "E14.35.0.2", {"start": v(93.93, 11.82) * mm, "end": v(92.76, 7.25) * mm});
            skLineSegment(sketch, "E14.35.0.3", {"start": v(93.93, 11.82) * mm, "end": v(96.16, 11.82) * mm});
            skLineSegment(sketch, "E14.36.0.0", {"start": v(97.33, 7.25) * mm, "end": v(99.57, 7.25) * mm});
            skLineSegment(sketch, "E14.36.0.1", {"start": v(102.97, 11.82) * mm, "end": v(104.14, 7.25) * mm});
            skLineSegment(sketch, "E14.36.0.2", {"start": v(100.74, 11.82) * mm, "end": v(99.57, 7.25) * mm});
            skLineSegment(sketch, "E14.36.0.3", {"start": v(100.74, 11.82) * mm, "end": v(102.97, 11.82) * mm});
            skLineSegment(sketch, "E14.37.0.0", {"start": v(104.14, 7.25) * mm, "end": v(106.38, 7.25) * mm});
            skLineSegment(sketch, "E14.37.0.1", {"start": v(109.78, 11.82) * mm, "end": v(110.95, 7.25) * mm});
            skLineSegment(sketch, "E14.37.0.2", {"start": v(107.54, 11.82) * mm, "end": v(106.38, 7.25) * mm});
            skLineSegment(sketch, "E14.37.0.3", {"start": v(107.54, 11.82) * mm, "end": v(109.78, 11.82) * mm});
            skLineSegment(sketch, "E14.38.0.0", {"start": v(110.95, 7.25) * mm, "end": v(113.18, 7.25) * mm});
            skLineSegment(sketch, "E14.38.0.1", {"start": v(116.59, 11.82) * mm, "end": v(117.75, 7.25) * mm});
            skLineSegment(sketch, "E14.38.0.2", {"start": v(114.35, 11.82) * mm, "end": v(113.18, 7.25) * mm});
            skLineSegment(sketch, "E14.38.0.3", {"start": v(114.35, 11.82) * mm, "end": v(116.59, 11.82) * mm});
            skLineSegment(sketch, "E14.39.0.0", {"start": v(117.75, 7.25) * mm, "end": v(119.99, 7.25) * mm});
            skLineSegment(sketch, "E14.39.0.1", {"start": v(123.4, 11.82) * mm, "end": v(124.56, 7.25) * mm});
            skLineSegment(sketch, "E14.39.0.2", {"start": v(121.16, 11.82) * mm, "end": v(119.99, 7.25) * mm});
            skLineSegment(sketch, "E14.39.0.3", {"start": v(121.16, 11.82) * mm, "end": v(123.4, 11.82) * mm});
            skLineSegment(sketch, "E14.40.0.0", {"start": v(124.56, 7.25) * mm, "end": v(126.8, 7.25) * mm});
            skLineSegment(sketch, "E14.40.0.1", {"start": v(130.2, 11.82) * mm, "end": v(131.37, 7.25) * mm});
            skLineSegment(sketch, "E14.40.0.2", {"start": v(127.97, 11.82) * mm, "end": v(126.8, 7.25) * mm});
            skLineSegment(sketch, "E14.40.0.3", {"start": v(127.97, 11.82) * mm, "end": v(130.2, 11.82) * mm});
            skLineSegment(sketch, "E14.41.0.0", {"start": v(131.37, 7.25) * mm, "end": v(133.6, 7.25) * mm});
            skLineSegment(sketch, "E14.41.0.1", {"start": v(137, 11.82) * mm, "end": v(138.18, 7.25) * mm});
            skLineSegment(sketch, "E14.41.0.2", {"start": v(134.77, 11.82) * mm, "end": v(133.6, 7.25) * mm});
            skLineSegment(sketch, "E14.41.0.3", {"start": v(134.77, 11.82) * mm, "end": v(137, 11.82) * mm});
            skLineSegment(sketch, "E14.42.0.0", {"start": v(138.18, 7.25) * mm, "end": v(140.41, 7.25) * mm});
            skLineSegment(sketch, "E14.42.0.1", {"start": v(143.81, 11.82) * mm, "end": v(144.98, 7.25) * mm});
            skLineSegment(sketch, "E14.42.0.2", {"start": v(141.58, 11.82) * mm, "end": v(140.41, 7.25) * mm});
            skLineSegment(sketch, "E14.42.0.3", {"start": v(141.58, 11.82) * mm, "end": v(143.81, 11.82) * mm});
            skLineSegment(sketch, "E14.43.0.0", {"start": v(144.98, 7.25) * mm, "end": v(147.22, 7.25) * mm});
            skLineSegment(sketch, "E14.43.0.1", {"start": v(150.62, 11.82) * mm, "end": v(151.8, 7.25) * mm});
            skLineSegment(sketch, "E14.43.0.2", {"start": v(148.39, 11.82) * mm, "end": v(147.22, 7.25) * mm});
            skLineSegment(sketch, "E14.43.0.3", {"start": v(148.39, 11.82) * mm, "end": v(150.62, 11.82) * mm});
            skLineSegment(sketch, "E14.44.0.0", {"start": v(151.8, 7.25) * mm, "end": v(154.03, 7.25) * mm});
            skLineSegment(sketch, "E14.44.0.1", {"start": v(157.43, 11.82) * mm, "end": v(158.6, 7.25) * mm});
            skLineSegment(sketch, "E14.44.0.2", {"start": v(155.2, 11.82) * mm, "end": v(154.03, 7.25) * mm});
            skLineSegment(sketch, "E14.44.0.3", {"start": v(155.2, 11.82) * mm, "end": v(157.43, 11.82) * mm});
            skLineSegment(sketch, "E14.45.0.0", {"start": v(158.6, 7.25) * mm, "end": v(160.83, 7.25) * mm});
            skLineSegment(sketch, "E14.45.0.1", {"start": v(164.24, 11.82) * mm, "end": v(165.4, 7.25) * mm});
            skLineSegment(sketch, "E14.45.0.2", {"start": v(162, 11.82) * mm, "end": v(160.83, 7.25) * mm});
            skLineSegment(sketch, "E14.45.0.3", {"start": v(162, 11.82) * mm, "end": v(164.24, 11.82) * mm});
            skLineSegment(sketch, "E14.46.0.0", {"start": v(165.4, 7.25) * mm, "end": v(167.64, 7.25) * mm});
            skLineSegment(sketch, "E14.46.0.1", {"start": v(171.04, 11.82) * mm, "end": v(172.21, 7.25) * mm});
            skLineSegment(sketch, "E14.46.0.2", {"start": v(168.8, 11.82) * mm, "end": v(167.64, 7.25) * mm});
            skLineSegment(sketch, "E14.46.0.3", {"start": v(168.8, 11.82) * mm, "end": v(171.04, 11.82) * mm});
            skLineSegment(sketch, "E14.47.0.0", {"start": v(172.21, 7.25) * mm, "end": v(174.45, 7.25) * mm});
            skLineSegment(sketch, "E14.47.0.1", {"start": v(177.85, 11.82) * mm, "end": v(179.02, 7.25) * mm});
            skLineSegment(sketch, "E14.47.0.2", {"start": v(175.62, 11.82) * mm, "end": v(174.45, 7.25) * mm});
            skLineSegment(sketch, "E14.47.0.3", {"start": v(175.62, 11.82) * mm, "end": v(177.85, 11.82) * mm});
            skLineSegment(sketch, "E14.48.0.0", {"start": v(179.02, 7.25) * mm, "end": v(181.25, 7.25) * mm});
            skLineSegment(sketch, "E14.48.0.1", {"start": v(184.66, 11.82) * mm, "end": v(185.83, 7.25) * mm});
            skLineSegment(sketch, "E14.48.0.2", {"start": v(182.42, 11.82) * mm, "end": v(181.25, 7.25) * mm});
            skLineSegment(sketch, "E14.48.0.3", {"start": v(182.42, 11.82) * mm, "end": v(184.66, 11.82) * mm});
            skLineSegment(sketch, "E14.49.0.0", {"start": v(185.83, 7.25) * mm, "end": v(188.06, 7.25) * mm});
            skLineSegment(sketch, "E14.49.0.1", {"start": v(191.47, 11.82) * mm, "end": v(192.63, 7.25) * mm});
            skLineSegment(sketch, "E14.49.0.2", {"start": v(189.23, 11.82) * mm, "end": v(188.06, 7.25) * mm});
            skLineSegment(sketch, "E14.49.0.3", {"start": v(189.23, 11.82) * mm, "end": v(191.47, 11.82) * mm});
            skLineSegment(sketch, "E14.direction1", {"start": v(-147.73, 7.25) * mm, "end": v(-140.92, 7.25) * mm, "construction": true});
            skLineSegment(sketch, "E15.1.0.0", {"start": v(192.63, 7.25) * mm, "end": v(194.87, 7.25) * mm});
            skLineSegment(sketch, "E15.1.0.1", {"start": v(198.27, 11.82) * mm, "end": v(199.44, 7.25) * mm});
            skLineSegment(sketch, "E15.1.0.2", {"start": v(196.04, 11.82) * mm, "end": v(194.87, 7.25) * mm});
            skLineSegment(sketch, "E15.1.0.3", {"start": v(196.04, 11.82) * mm, "end": v(198.27, 11.82) * mm});
            skLineSegment(sketch, "E15.2.0.0", {"start": v(199.44, 7.25) * mm, "end": v(201.68, 7.25) * mm});
            skLineSegment(sketch, "E15.2.0.1", {"start": v(205.08, 11.82) * mm, "end": v(206.25, 7.25) * mm});
            skLineSegment(sketch, "E15.2.0.2", {"start": v(202.84, 11.82) * mm, "end": v(201.68, 7.25) * mm});
            skLineSegment(sketch, "E15.2.0.3", {"start": v(202.84, 11.82) * mm, "end": v(205.08, 11.82) * mm});
            skLineSegment(sketch, "E15.3.0.0", {"start": v(206.25, 7.25) * mm, "end": v(208.48, 7.25) * mm});
            skLineSegment(sketch, "E15.3.0.1", {"start": v(211.89, 11.82) * mm, "end": v(213.06, 7.25) * mm});
            skLineSegment(sketch, "E15.3.0.2", {"start": v(209.65, 11.82) * mm, "end": v(208.48, 7.25) * mm});
            skLineSegment(sketch, "E15.3.0.3", {"start": v(209.65, 11.82) * mm, "end": v(211.89, 11.82) * mm});
            skLineSegment(sketch, "E15.4.0.0", {"start": v(213.06, 7.25) * mm, "end": v(215.3, 7.25) * mm});
            skLineSegment(sketch, "E15.4.0.1", {"start": v(218.7, 11.82) * mm, "end": v(219.86, 7.25) * mm});
            skLineSegment(sketch, "E15.4.0.2", {"start": v(216.46, 11.82) * mm, "end": v(215.3, 7.25) * mm});
            skLineSegment(sketch, "E15.4.0.3", {"start": v(216.46, 11.82) * mm, "end": v(218.7, 11.82) * mm});
            skLineSegment(sketch, "E15.5.0.0", {"start": v(219.86, 7.25) * mm, "end": v(222.1, 7.25) * mm});
            skLineSegment(sketch, "E15.5.0.1", {"start": v(225.5, 11.82) * mm, "end": v(226.67, 7.25) * mm});
            skLineSegment(sketch, "E15.5.0.2", {"start": v(223.27, 11.82) * mm, "end": v(222.1, 7.25) * mm});
            skLineSegment(sketch, "E15.5.0.3", {"start": v(223.27, 11.82) * mm, "end": v(225.5, 11.82) * mm});
            skLineSegment(sketch, "E15.6.0.0", {"start": v(226.67, 7.25) * mm, "end": v(228.9, 7.25) * mm});
            skLineSegment(sketch, "E15.6.0.1", {"start": v(232.3, 11.82) * mm, "end": v(233.48, 7.25) * mm});
            skLineSegment(sketch, "E15.6.0.2", {"start": v(230.07, 11.82) * mm, "end": v(228.9, 7.25) * mm});
            skLineSegment(sketch, "E15.6.0.3", {"start": v(230.07, 11.82) * mm, "end": v(232.3, 11.82) * mm});
            skLineSegment(sketch, "E15.7.0.0", {"start": v(233.48, 7.25) * mm, "end": v(235.71, 7.25) * mm});
            skLineSegment(sketch, "E15.7.0.1", {"start": v(239.12, 11.82) * mm, "end": v(240.28, 7.25) * mm});
            skLineSegment(sketch, "E15.7.0.2", {"start": v(236.88, 11.82) * mm, "end": v(235.71, 7.25) * mm});
            skLineSegment(sketch, "E15.7.0.3", {"start": v(236.88, 11.82) * mm, "end": v(239.12, 11.82) * mm});
            skLineSegment(sketch, "E15.8.0.0", {"start": v(240.28, 7.25) * mm, "end": v(242.52, 7.25) * mm});
            skLineSegment(sketch, "E15.8.0.1", {"start": v(245.92, 11.82) * mm, "end": v(247.1, 7.25) * mm});
            skLineSegment(sketch, "E15.8.0.2", {"start": v(243.69, 11.82) * mm, "end": v(242.52, 7.25) * mm});
            skLineSegment(sketch, "E15.8.0.3", {"start": v(243.69, 11.82) * mm, "end": v(245.92, 11.82) * mm});
            skLineSegment(sketch, "E15.9.0.0", {"start": v(247.1, 7.25) * mm, "end": v(249.33, 7.25) * mm});
            skLineSegment(sketch, "E15.9.0.1", {"start": v(252.73, 11.82) * mm, "end": v(253.9, 7.25) * mm});
            skLineSegment(sketch, "E15.9.0.2", {"start": v(250.5, 11.82) * mm, "end": v(249.33, 7.25) * mm});
            skLineSegment(sketch, "E15.9.0.3", {"start": v(250.5, 11.82) * mm, "end": v(252.73, 11.82) * mm});
            skLineSegment(sketch, "E15.10.0.0", {"start": v(253.9, 7.25) * mm, "end": v(256.13, 7.25) * mm});
            skLineSegment(sketch, "E15.10.0.1", {"start": v(259.54, 11.82) * mm, "end": v(260.7, 7.25) * mm});
            skLineSegment(sketch, "E15.10.0.2", {"start": v(257.3, 11.82) * mm, "end": v(256.13, 7.25) * mm});
            skLineSegment(sketch, "E15.10.0.3", {"start": v(257.3, 11.82) * mm, "end": v(259.54, 11.82) * mm});
            skLineSegment(sketch, "E15.11.0.0", {"start": v(260.7, 7.25) * mm, "end": v(262.94, 7.25) * mm});
            skLineSegment(sketch, "E15.11.0.1", {"start": v(266.34, 11.82) * mm, "end": v(267.51, 7.25) * mm});
            skLineSegment(sketch, "E15.11.0.2", {"start": v(264.1, 11.82) * mm, "end": v(262.94, 7.25) * mm});
            skLineSegment(sketch, "E15.11.0.3", {"start": v(264.1, 11.82) * mm, "end": v(266.34, 11.82) * mm});
            skLineSegment(sketch, "E15.12.0.0", {"start": v(267.51, 7.25) * mm, "end": v(269.75, 7.25) * mm});
            skLineSegment(sketch, "E15.12.0.1", {"start": v(273.15, 11.82) * mm, "end": v(274.32, 7.25) * mm});
            skLineSegment(sketch, "E15.12.0.2", {"start": v(270.92, 11.82) * mm, "end": v(269.75, 7.25) * mm});
            skLineSegment(sketch, "E15.12.0.3", {"start": v(270.92, 11.82) * mm, "end": v(273.15, 11.82) * mm});
            skLineSegment(sketch, "E15.13.0.0", {"start": v(274.32, 7.25) * mm, "end": v(276.56, 7.25) * mm});
            skLineSegment(sketch, "E15.13.0.1", {"start": v(279.96, 11.82) * mm, "end": v(281.13, 7.25) * mm});
            skLineSegment(sketch, "E15.13.0.2", {"start": v(277.72, 11.82) * mm, "end": v(276.56, 7.25) * mm});
            skLineSegment(sketch, "E15.13.0.3", {"start": v(277.72, 11.82) * mm, "end": v(279.96, 11.82) * mm});
            skLineSegment(sketch, "E15.14.0.0", {"start": v(281.13, 7.25) * mm, "end": v(283.36, 7.25) * mm});
            skLineSegment(sketch, "E15.14.0.1", {"start": v(286.77, 11.82) * mm, "end": v(287.93, 7.25) * mm});
            skLineSegment(sketch, "E15.14.0.2", {"start": v(284.53, 11.82) * mm, "end": v(283.36, 7.25) * mm});
            skLineSegment(sketch, "E15.14.0.3", {"start": v(284.53, 11.82) * mm, "end": v(286.77, 11.82) * mm});
            skLineSegment(sketch, "E15.15.0.0", {"start": v(287.93, 7.25) * mm, "end": v(290.17, 7.25) * mm});
            skLineSegment(sketch, "E15.15.0.1", {"start": v(293.57, 11.82) * mm, "end": v(294.74, 7.25) * mm});
            skLineSegment(sketch, "E15.15.0.2", {"start": v(291.34, 11.82) * mm, "end": v(290.17, 7.25) * mm});
            skLineSegment(sketch, "E15.15.0.3", {"start": v(291.34, 11.82) * mm, "end": v(293.57, 11.82) * mm});
            skLineSegment(sketch, "E15.16.0.0", {"start": v(294.74, 7.25) * mm, "end": v(296.98, 7.25) * mm});
            skLineSegment(sketch, "E15.16.0.1", {"start": v(300.38, 11.82) * mm, "end": v(301.55, 7.25) * mm});
            skLineSegment(sketch, "E15.16.0.2", {"start": v(298.15, 11.82) * mm, "end": v(296.98, 7.25) * mm});
            skLineSegment(sketch, "E15.16.0.3", {"start": v(298.15, 11.82) * mm, "end": v(300.38, 11.82) * mm});
            skLineSegment(sketch, "E15.17.0.0", {"start": v(301.55, 7.25) * mm, "end": v(303.78, 7.25) * mm});
            skLineSegment(sketch, "E15.17.0.1", {"start": v(307.19, 11.82) * mm, "end": v(308.36, 7.25) * mm});
            skLineSegment(sketch, "E15.17.0.2", {"start": v(304.95, 11.82) * mm, "end": v(303.78, 7.25) * mm});
            skLineSegment(sketch, "E15.17.0.3", {"start": v(304.95, 11.82) * mm, "end": v(307.19, 11.82) * mm});
            skLineSegment(sketch, "E15.18.0.0", {"start": v(308.36, 7.25) * mm, "end": v(310.6, 7.25) * mm});
            skLineSegment(sketch, "E15.18.0.1", {"start": v(314, 11.82) * mm, "end": v(315.16, 7.25) * mm});
            skLineSegment(sketch, "E15.18.0.2", {"start": v(311.76, 11.82) * mm, "end": v(310.6, 7.25) * mm});
            skLineSegment(sketch, "E15.18.0.3", {"start": v(311.76, 11.82) * mm, "end": v(314, 11.82) * mm});
            skLineSegment(sketch, "E15.19.0.0", {"start": v(315.16, 7.25) * mm, "end": v(317.4, 7.25) * mm});
            skLineSegment(sketch, "E15.19.0.1", {"start": v(320.8, 11.82) * mm, "end": v(321.97, 7.25) * mm});
            skLineSegment(sketch, "E15.19.0.2", {"start": v(318.57, 11.82) * mm, "end": v(317.4, 7.25) * mm});
            skLineSegment(sketch, "E15.19.0.3", {"start": v(318.57, 11.82) * mm, "end": v(320.8, 11.82) * mm});
            skLineSegment(sketch, "E15.20.0.0", {"start": v(321.97, 7.25) * mm, "end": v(324.2, 7.25) * mm});
            skLineSegment(sketch, "E15.20.0.1", {"start": v(327.6, 11.82) * mm, "end": v(328.78, 7.25) * mm});
            skLineSegment(sketch, "E15.20.0.2", {"start": v(325.37, 11.82) * mm, "end": v(324.2, 7.25) * mm});
            skLineSegment(sketch, "E15.20.0.3", {"start": v(325.37, 11.82) * mm, "end": v(327.6, 11.82) * mm});
            skLineSegment(sketch, "E15.21.0.0", {"start": v(328.78, 7.25) * mm, "end": v(331.01, 7.25) * mm});
            skLineSegment(sketch, "E15.21.0.1", {"start": v(334.42, 11.82) * mm, "end": v(335.58, 7.25) * mm});
            skLineSegment(sketch, "E15.21.0.2", {"start": v(332.18, 11.82) * mm, "end": v(331.01, 7.25) * mm});
            skLineSegment(sketch, "E15.21.0.3", {"start": v(332.18, 11.82) * mm, "end": v(334.42, 11.82) * mm});
            skLineSegment(sketch, "E15.22.0.0", {"start": v(335.58, 7.25) * mm, "end": v(337.82, 7.25) * mm});
            skLineSegment(sketch, "E15.22.0.1", {"start": v(341.22, 11.82) * mm, "end": v(342.4, 7.25) * mm});
            skLineSegment(sketch, "E15.22.0.2", {"start": v(338.99, 11.82) * mm, "end": v(337.82, 7.25) * mm});
            skLineSegment(sketch, "E15.22.0.3", {"start": v(338.99, 11.82) * mm, "end": v(341.22, 11.82) * mm});
            skLineSegment(sketch, "E15.23.0.0", {"start": v(342.4, 7.25) * mm, "end": v(344.63, 7.25) * mm});
            skLineSegment(sketch, "E15.23.0.1", {"start": v(348.03, 11.82) * mm, "end": v(349.2, 7.25) * mm});
            skLineSegment(sketch, "E15.23.0.2", {"start": v(345.8, 11.82) * mm, "end": v(344.63, 7.25) * mm});
            skLineSegment(sketch, "E15.23.0.3", {"start": v(345.8, 11.82) * mm, "end": v(348.03, 11.82) * mm});
            skLineSegment(sketch, "E15.24.0.0", {"start": v(349.2, 7.25) * mm, "end": v(351.43, 7.25) * mm});
            skLineSegment(sketch, "E15.24.0.1", {"start": v(354.84, 11.82) * mm, "end": v(356, 7.25) * mm});
            skLineSegment(sketch, "E15.24.0.2", {"start": v(352.6, 11.82) * mm, "end": v(351.43, 7.25) * mm});
            skLineSegment(sketch, "E15.24.0.3", {"start": v(352.6, 11.82) * mm, "end": v(354.84, 11.82) * mm});
            skLineSegment(sketch, "E15.25.0.0", {"start": v(356, 7.25) * mm, "end": v(358.24, 7.25) * mm});
            skLineSegment(sketch, "E15.25.0.1", {"start": v(361.65, 11.82) * mm, "end": v(362.81, 7.25) * mm});
            skLineSegment(sketch, "E15.25.0.2", {"start": v(359.41, 11.82) * mm, "end": v(358.24, 7.25) * mm});
            skLineSegment(sketch, "E15.25.0.3", {"start": v(359.41, 11.82) * mm, "end": v(361.65, 11.82) * mm});
            skLineSegment(sketch, "E15.26.0.0", {"start": v(362.81, 7.25) * mm, "end": v(365.05, 7.25) * mm});
            skLineSegment(sketch, "E15.26.0.1", {"start": v(368.45, 11.82) * mm, "end": v(369.62, 7.25) * mm});
            skLineSegment(sketch, "E15.26.0.2", {"start": v(366.22, 11.82) * mm, "end": v(365.05, 7.25) * mm});
            skLineSegment(sketch, "E15.26.0.3", {"start": v(366.22, 11.82) * mm, "end": v(368.45, 11.82) * mm});
            skLineSegment(sketch, "E15.27.0.0", {"start": v(369.62, 7.25) * mm, "end": v(371.86, 7.25) * mm});
            skLineSegment(sketch, "E15.27.0.1", {"start": v(375.26, 11.82) * mm, "end": v(376.43, 7.25) * mm});
            skLineSegment(sketch, "E15.27.0.2", {"start": v(373.02, 11.82) * mm, "end": v(371.86, 7.25) * mm});
            skLineSegment(sketch, "E15.27.0.3", {"start": v(373.02, 11.82) * mm, "end": v(375.26, 11.82) * mm});
            skLineSegment(sketch, "E15.28.0.0", {"start": v(376.43, 7.25) * mm, "end": v(378.66, 7.25) * mm});
            skLineSegment(sketch, "E15.28.0.1", {"start": v(382.07, 11.82) * mm, "end": v(383.24, 7.25) * mm});
            skLineSegment(sketch, "E15.28.0.2", {"start": v(379.83, 11.82) * mm, "end": v(378.66, 7.25) * mm});
            skLineSegment(sketch, "E15.28.0.3", {"start": v(379.83, 11.82) * mm, "end": v(382.07, 11.82) * mm});
            skLineSegment(sketch, "E15.29.0.0", {"start": v(383.24, 7.25) * mm, "end": v(385.47, 7.25) * mm});
            skLineSegment(sketch, "E15.29.0.1", {"start": v(388.87, 11.82) * mm, "end": v(390.04, 7.25) * mm});
            skLineSegment(sketch, "E15.29.0.2", {"start": v(386.64, 11.82) * mm, "end": v(385.47, 7.25) * mm});
            skLineSegment(sketch, "E15.29.0.3", {"start": v(386.64, 11.82) * mm, "end": v(388.87, 11.82) * mm});
            skLineSegment(sketch, "E15.30.0.0", {"start": v(390.04, 7.25) * mm, "end": v(392.28, 7.25) * mm});
            skLineSegment(sketch, "E15.30.0.1", {"start": v(395.68, 11.82) * mm, "end": v(396.85, 7.25) * mm});
            skLineSegment(sketch, "E15.30.0.2", {"start": v(393.45, 11.82) * mm, "end": v(392.28, 7.25) * mm});
            skLineSegment(sketch, "E15.30.0.3", {"start": v(393.45, 11.82) * mm, "end": v(395.68, 11.82) * mm});
            skLineSegment(sketch, "E15.31.0.0", {"start": v(396.85, 7.25) * mm, "end": v(399.08, 7.25) * mm});
            skLineSegment(sketch, "E15.31.0.1", {"start": v(402.49, 11.82) * mm, "end": v(403.66, 7.25) * mm});
            skLineSegment(sketch, "E15.31.0.2", {"start": v(400.25, 11.82) * mm, "end": v(399.08, 7.25) * mm});
            skLineSegment(sketch, "E15.31.0.3", {"start": v(400.25, 11.82) * mm, "end": v(402.49, 11.82) * mm});
            skLineSegment(sketch, "E15.32.0.0", {"start": v(403.66, 7.25) * mm, "end": v(405.9, 7.25) * mm});
            skLineSegment(sketch, "E15.direction1", {"start": v(185.83, 7.25) * mm, "end": v(192.63, 7.25) * mm, "construction": true});
            skSolve(sketch);
        }
        {
            var Q0;
            Q0 = qSketchRegion(id + "F2", true);
            extrude(context, id + "F3", {"entities" : qUnion([Q0]), "operationType" : NewBodyOperationType.ADD, "oppositeDirection" : true, "depth" : 19.05 * mm});
        }
        {
            var Q0;
            Q0=makeQuery(id+"F1.opExtrude","SWEPT_FACE",FACE,{"disambiguationData":[OSD([sQuery(id+"F0.wireOp",EDGE,"E0.top")])]});
            var sketch = newSketch(context, id + "F4", { "sketchPlane" : qUnion([Q0])});
            skLineSegment(sketch, "E16.0", {"start": v(-406.4, 9.53) * mm, "end": v(-406.4, -9.52) * mm, "construction": true});
            skLineSegment(sketch, "E17.0", {"start": v(-342.9, 9.53) * mm, "end": v(-342.9, -9.52) * mm, "construction": true});
            skPoint(sketch, "E18", {"position": v(-342.9, 0) * mm});
            skPoint(sketch, "E19.1.0.0", {"position": v(-114.3, 0) * mm});
            skPoint(sketch, "E19.2.0.0", {"position": v(114.3, 0) * mm});
            skPoint(sketch, "E19.3.0.0", {"position": v(342.9, 0) * mm});
            skLineSegment(sketch, "E19.direction1", {"start": v(-342.9, 0) * mm, "end": v(-114.3, 0) * mm, "construction": true});
            skSolve(sketch);
        }
        {
            var Q0;
            Q0=sQuery(id+"F4.wireOp",VERTEX,"E18");
            var Q1;
            Q1=sQuery(id+"F4.wireOp",VERTEX,"E19.1.0.0");
            var Q2;
            Q2=sQuery(id+"F4.wireOp",VERTEX,"E19.2.0.0");
            var Q3;
            Q3=sQuery(id+"F4.wireOp",VERTEX,"E19.3.0.0");
            var Q4;
            Q4=makeQuery(id+"F1.opExtrude","SWEPT_BODY",BODY,{"disambiguationData":[OSD([sQuery(id+"F0.wireOp",EDGE,"E0.bottom"),sQuery(id+"F0.wireOp",EDGE,"E0.top"),sQuery(id+"F0.wireOp",EDGE,"E0.left"),sQuery(id+"F0.wireOp",EDGE,"E0.right")])]});
            hole(context, id + "F5", {"style" : HoleStyle.SIMPLE, "endStyle" : HoleEndStyle.THROUGH, "standardTappedOrClearance" : lookupTablePath({ "standard" : "ANSI", "engagement" : "75%", "pitch" : "16 tpi", "size" : "3/8", "type" : "Tapped" }), "standardBlindInLast" : lookupTablePath({ "standard" : "ANSI", "engagement" : "75%", "pitch" : "16 tpi", "size" : "3/8", "type" : "Tapped" }), "holeDiameter" : 7.94 * mm, "locations" : qUnion([Q0, Q1, Q2, Q3]), "scope" : qUnion([Q4]), "isTappedThrough" : true, "majorDiameter" : 9.53 * mm, "showTappedDepth" : true});
        }
    });
